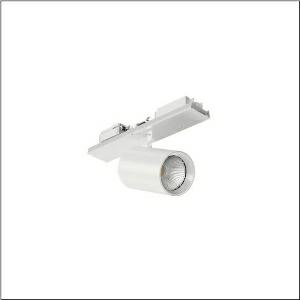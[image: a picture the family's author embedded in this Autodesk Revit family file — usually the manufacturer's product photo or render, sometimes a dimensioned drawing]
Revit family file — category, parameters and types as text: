
# Revit family: licross_r__spot_31_51sl137a35b_e6ce
name_source: partatom
category: Lighting Fixtures
units: mm (PartAtom-declared; Revit-internal decimal feet)

## family parameters
Cut with Voids When Loaded = No
Host = Face
Light Source = No
Part Type = Normal
Room Calculation Point = No
Round Connector Dimension = Use Diameter
Shared = No

## types (1)
- --- (1 x LED, 5030 lm, 42.5 W, 3000K)
    Apparent Load = 43 VA
    CIE Flux Codes = 92 97 99 100 100
    Color Rendering = 90
    Color Temperature = 3000K
    Default Elevation = 1800 mm
    Description = Licross® Spot 31, directional spotlight, light control with lens, of plastic, LED rated luminous flux: 5.030lm, light colour: 930, with plug, 3-pole, with phase selection, mains connection: 220..240V, AC, 50/60Hz, of aluminium, traffic white (RAL 9016), length: 300mm, diameter: 90mm, protection rating (complete): IP20, insulation class (complete): insulation class I (protective earthing), certification: CE, packaging unit: 1 piece
    Height = 175 mm
    Lamp = 1 x LED
    Lamp Light Flux = 5030 lm
    Lamp Power = 42.5 W
    Lamp count = 1
    Length = 90 mm
    Luminous efficacy = 118 lm/W
    Manufacturer = Siteco
    ModVariant = No
    Model = 51SL137A35B
    Mounting Place = Ceiling
    Mounting Type = Pendant
    Number of Poles = 1
    OnlyDefault = Yes
    Power Factor = 1
    Product Name = Licross® Spot 31
    Product group = directional spotlight
    ProductGroupID = 905
    Protection Class = Protection class I
    Protection Degree = IP 20
    RLX_Detail_Level = 1
    RLX_Emergency_Light_Flux = 0 lm
    RLX_Emergency_Type = 0
    RLX_Emergency_Type_DB = No
    RlxData = <blob elided: 14821 chars, md5=af6e1df7>
    Socket = socket
    Standby Power = 0 W
    System Light Flux = 5030 lm
    System Power = 43 W
    Type Comments = factory setting: luminous flux: 100 % | (ON | ON | ON) | 1050 mA
    Type Image = l_1245720.jpg
    URL = http://relux.com
    VarID = @adj_153823
    Voltage = 0 V
    Weight = 0.00 kg
    Width = 0 mm  [stored 0 ft]

note: [stored X ft] marks values corroborated as IEEE doubles in the binary element streams (Revit-internal decimal feet)

## geometry (parser evidence)
native form markers: Sweep x13
no freeform markers — native parametric forms only
